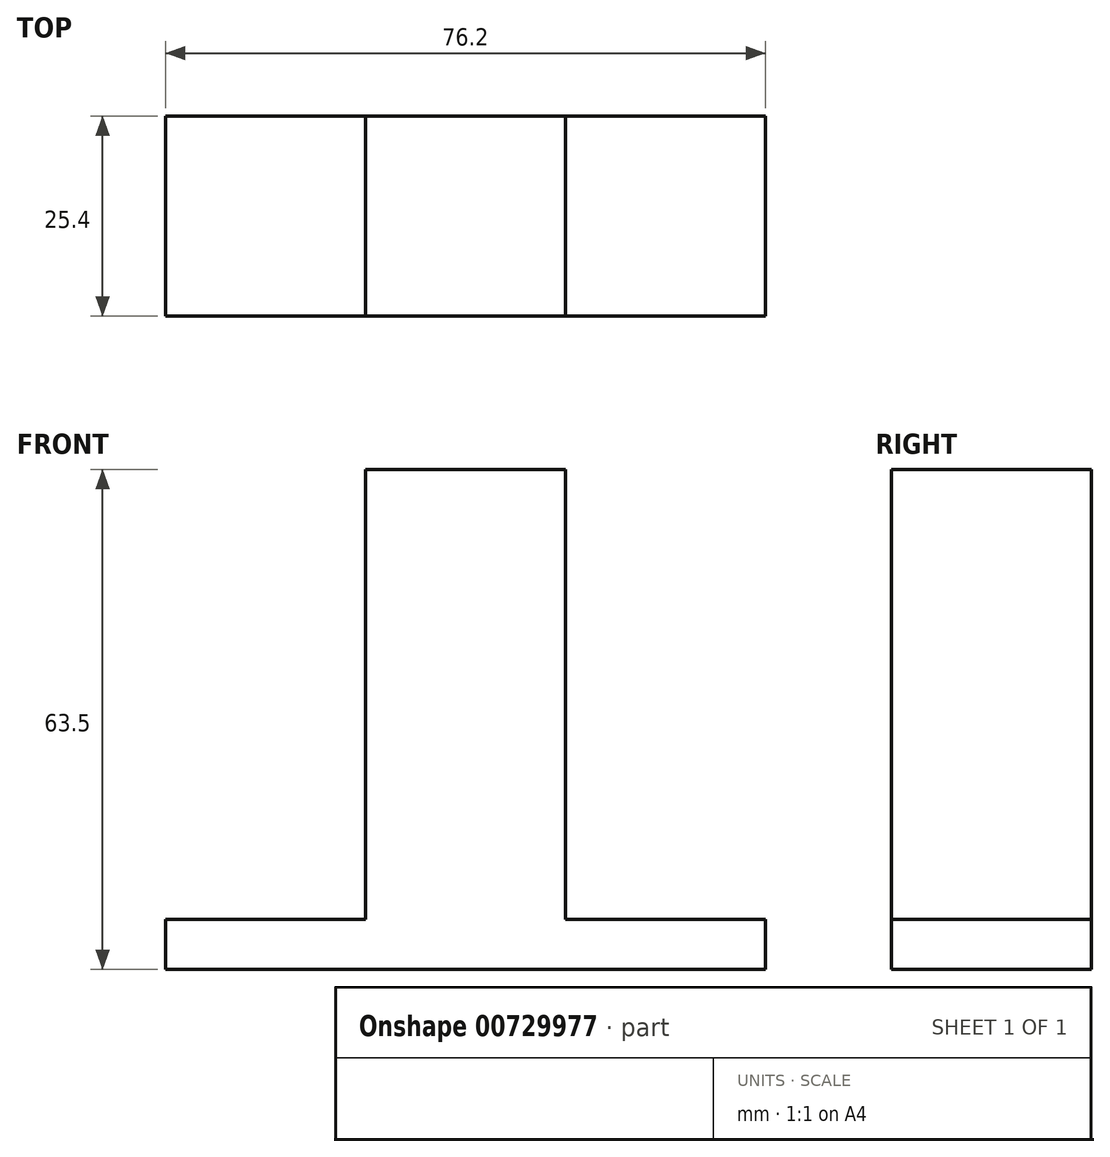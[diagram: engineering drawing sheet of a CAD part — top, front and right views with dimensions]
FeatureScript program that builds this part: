
annotation { "Feature Type Name" : "Feature", "Feature Type Description" : "" }
export const myFeature = defineFeature(function(context is Context, id is Id, definition is map)
    precondition{}
    {
        {
            var Q0;
            Q0=qCreatedBy(makeId("Front.planeOp"),FACE);
            var sketch = newSketch(context, id + "F0", { "sketchPlane" : qUnion([Q0])});
            skLineSegment(sketch, "E0", {"start": v(-38.1, 0) * mm, "end": v(38.1, 0) * mm});
            skLineSegment(sketch, "E1", {"start": v(38.1, 0) * mm, "end": v(38.1, 6.35) * mm});
            skLineSegment(sketch, "E2", {"start": v(38.1, 6.35) * mm, "end": v(12.7, 6.35) * mm});
            skLineSegment(sketch, "E3", {"start": v(12.7, 6.35) * mm, "end": v(12.7, 63.5) * mm});
            skLineSegment(sketch, "E4", {"start": v(12.7, 63.5) * mm, "end": v(-12.7, 63.5) * mm});
            skLineSegment(sketch, "E5", {"start": v(-12.7, 63.5) * mm, "end": v(-12.7, 6.35) * mm});
            skLineSegment(sketch, "E6", {"start": v(-12.7, 6.35) * mm, "end": v(-38.1, 6.35) * mm});
            skLineSegment(sketch, "E7", {"start": v(-38.1, 6.35) * mm, "end": v(-38.1, 0) * mm});
            skLineSegment(sketch, "E8", {"start": v(0, 0) * mm, "end": v(0, 63.5) * mm, "construction": true});
            skSolve(sketch);
        }
        {
            var Q0;
            Q0 = qSketchRegion(id + "F0", true);
            extrude(context, id + "F1", {"entities" : qUnion([Q0]), "endBound" : BoundingType.SYMMETRIC, "depth" : 25.4 * mm, "offsetDistance" : 25.4 * mm});
        }
    });
